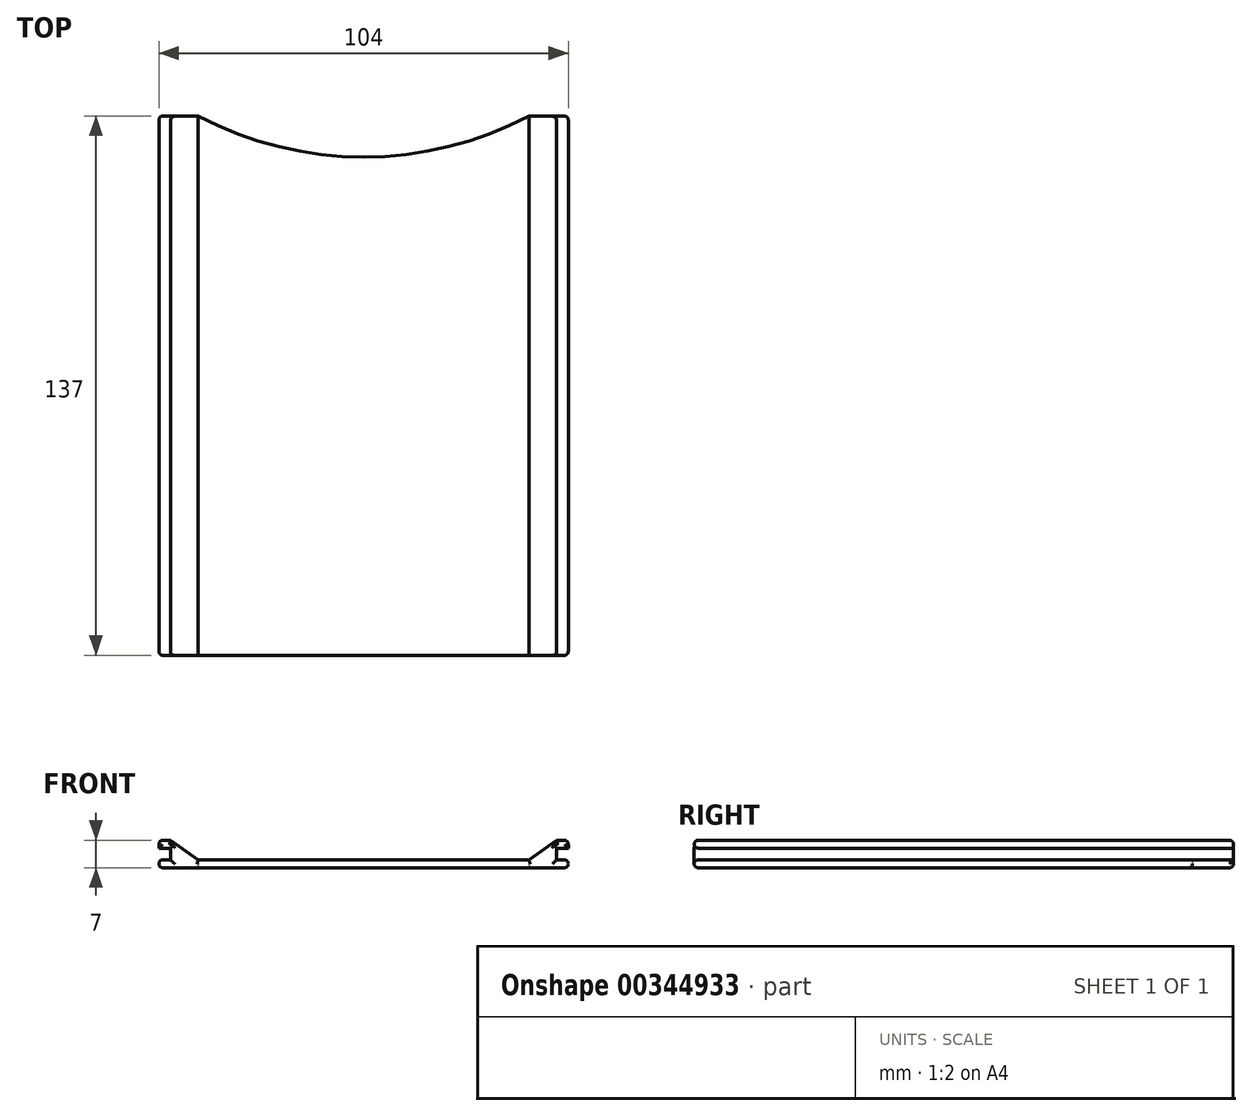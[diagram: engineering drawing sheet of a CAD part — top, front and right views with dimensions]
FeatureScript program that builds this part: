
annotation { "Feature Type Name" : "Feature", "Feature Type Description" : "" }
export const myFeature = defineFeature(function(context is Context, id is Id, definition is map)
    precondition{}
    {
        {
            var Q0;
            Q0=qCreatedBy(makeId("Top.planeOp"),FACE);
            var sketch = newSketch(context, id + "F0", { "sketchPlane" : qUnion([Q0])});
            skLineSegment(sketch, "E0", {"start": v(0, 0) * mm, "end": v(0, -68.5) * mm});
            skLineSegment(sketch, "E1", {"start": v(0, -68.5) * mm, "end": v(-52, -68.5) * mm});
            skLineSegment(sketch, "E2", {"start": v(-52, -68.5) * mm, "end": v(-52, 68.5) * mm});
            skLineSegment(sketch, "E3", {"start": v(-52, 68.5) * mm, "end": v(-42, 68.5) * mm});
            skLineSegment(sketch, "E4", {"start": v(0, -68.5) * mm, "end": v(52, -68.5) * mm});
            skLineSegment(sketch, "E5", {"start": v(52, -68.5) * mm, "end": v(52, 68.5) * mm});
            skLineSegment(sketch, "E6", {"start": v(52, 68.5) * mm, "end": v(42, 68.5) * mm});
            skArc(sketch, "E7", {"start": v(-42, 68.5) * mm, "mid": v(0, 58.1) * mm, "end": v(42, 68.5) * mm});
            skSolve(sketch);
        }
        {
            var Q0;
            Q0=makeQuery(id+"F0.imprint","IMPRINT",FACE,{"disambiguationData":[TD([[makeQuery(id+"F0.imprint","IMPRINT",EDGE,{"derivedFrom":sQuery(id+"F0.wireOp",EDGE,"E1")}),-1.0]])]});
            extrude(context, id + "F1", {"entities" : qUnion([Q0]), "depth" : 2 * mm});
        }
        {
            var Q0;
            Q0=makeQuery(id+"F1.opExtrude","CAP_FACE",FACE,{"disambiguationData":[OSD([sQuery(id+"F0.wireOp",EDGE,"E1"),sQuery(id+"F0.wireOp",EDGE,"E2"),sQuery(id+"F0.wireOp",EDGE,"E3"),sQuery(id+"F0.wireOp",EDGE,"E4"),sQuery(id+"F0.wireOp",EDGE,"E5"),sQuery(id+"F0.wireOp",EDGE,"E6"),sQuery(id+"F0.wireOp",EDGE,"E7")])],"isStart":false});
            var sketch = newSketch(context, id + "F2", { "sketchPlane" : qUnion([Q0])});
            skLineSegment(sketch, "E8.0", {"start": v(-42, -68.5) * mm, "end": v(-42, 68.5) * mm});
            skLineSegment(sketch, "E9.0", {"start": v(42, -68.5) * mm, "end": v(42, 68.5) * mm});
            skSolve(sketch);
        }
        {
            var Q0;
            {var subQ0=sQuery(id+"F2.wireOp",EDGE,"E8.0");Q0=makeQuery(id+"F2.imprint","IMPRINT",FACE,{"disambiguationData":[TD([[makeQuery(id+"F2.imprint","IMPRINT",EDGE,{"derivedFrom":subQ0}),1.0]])]});}
            var Q1;
            {var subQ0=sQuery(id+"F2.wireOp",EDGE,"E9.0");Q1=makeQuery(id+"F2.imprint","IMPRINT",FACE,{"disambiguationData":[TD([[makeQuery(id+"F2.imprint","IMPRINT",EDGE,{"derivedFrom":subQ0}),-1.0]])]});}
            extrude(context, id + "F3", {"entities" : qUnion([Q0, Q1]), "operationType" : NewBodyOperationType.ADD, "depth" : 5 * mm});
        }
        {
            var Q0;
            {var subQ0=sQuery(id+"F0.wireOp",EDGE,"E2");Q0=makeQuery(id+"F3.boolean.opBoolean","MERGE",FACE,{"derivedFrom":[makeQuery(id+"F1.opExtrude","SWEPT_FACE",FACE,{"disambiguationData":[OSD([subQ0])]}),makeQuery(id+"F3.opExtrude","SWEPT_FACE",FACE,{"disambiguationData":[OSD([subQ0])]})]});}
            var sketch = newSketch(context, id + "F4", { "sketchPlane" : qUnion([Q0])});
            skLineSegment(sketch, "E10.0", {"start": v(68.5, 5) * mm, "end": v(-68.5, 5) * mm});
            skLineSegment(sketch, "E11.0", {"start": v(68.5, 2) * mm, "end": v(-68.5, 2) * mm});
            skSolve(sketch);
        }
        {
            var Q0;
            {var subQ0=sQuery(id+"F4.wireOp",EDGE,"E10.0");Q0=makeQuery(id+"F4.imprint","IMPRINT",FACE,{"disambiguationData":[TD([[makeQuery(id+"F4.imprint","IMPRINT",EDGE,{"derivedFrom":subQ0}),1.0]])]});}
            extrude(context, id + "F5", {"entities" : qUnion([Q0]), "operationType" : NewBodyOperationType.REMOVE, "oppositeDirection" : true, "depth" : 3 * mm});
        }
        {
            var Q0;
            {var subQ0=sQuery(id+"F0.wireOp",EDGE,"E5");Q0=makeQuery(id+"F3.boolean.opBoolean","MERGE",FACE,{"derivedFrom":[makeQuery(id+"F1.opExtrude","SWEPT_FACE",FACE,{"disambiguationData":[OSD([subQ0])]}),makeQuery(id+"F3.opExtrude","SWEPT_FACE",FACE,{"disambiguationData":[OSD([subQ0])]})]});}
            var sketch = newSketch(context, id + "F6", { "sketchPlane" : qUnion([Q0])});
            skLineSegment(sketch, "E12.0", {"start": v(-68.5, 5) * mm, "end": v(68.5, 5) * mm});
            skLineSegment(sketch, "E13.0", {"start": v(-68.5, 2) * mm, "end": v(68.5, 2) * mm});
            skSolve(sketch);
        }
        {
            var Q0;
            {var subQ0=sQuery(id+"F6.wireOp",EDGE,"E12.0");Q0=makeQuery(id+"F6.imprint","IMPRINT",FACE,{"disambiguationData":[TD([[makeQuery(id+"F6.imprint","IMPRINT",EDGE,{"derivedFrom":subQ0}),-1.0]])]});}
            extrude(context, id + "F7", {"entities" : qUnion([Q0]), "operationType" : NewBodyOperationType.REMOVE, "oppositeDirection" : true, "depth" : 3 * mm});
        }
        {
            var Q0;
            Q0=makeQuery(id+"F3.opExtrude","CAP_EDGE",EDGE,{"disambiguationData":[OSD([sQuery(id+"F2.wireOp",EDGE,"E8.0")])],"isStart":false});
            chamfer(context, id + "F8", {"entities" : qUnion([Q0]), "chamferType" : ChamferType.TWO_OFFSETS, "width1" : 7 * mm, "oppositeDirection" : false, "width2" : 5 * mm, "tangentPropagation" : true});
        }
        {
            var Q0;
            Q0=makeQuery(id+"F3.opExtrude","CAP_EDGE",EDGE,{"disambiguationData":[OSD([sQuery(id+"F2.wireOp",EDGE,"E9.0")])],"isStart":false});
            chamfer(context, id + "F9", {"entities" : qUnion([Q0]), "chamferType" : ChamferType.TWO_OFFSETS, "width1" : 5 * mm, "oppositeDirection" : false, "width2" : 7 * mm, "tangentPropagation" : true});
        }
        {
            var Q0;
            Q0=makeQuery(id+"F7.boolean.opBoolean","COPY",EDGE,{"derivedFrom":makeQuery(id+"F7.opExtrude","CAP_EDGE",EDGE,{"disambiguationData":[OSD([sQuery(id+"F6.wireOp",EDGE,"E13.0")])],"isStart":true})});
            var Q1;
            Q1=makeQuery(id+"F1.opExtrude","CAP_EDGE",EDGE,{"disambiguationData":[OSD([sQuery(id+"F0.wireOp",EDGE,"E5")])],"isStart":true});
            var Q2;
            Q2=makeQuery(id+"F3.opExtrude","CAP_EDGE",EDGE,{"disambiguationData":[OSD([sQuery(id+"F0.wireOp",EDGE,"E5")])],"isStart":false});
            var Q3;
            Q3=makeQuery(id+"F7.boolean.opBoolean","COPY",EDGE,{"derivedFrom":makeQuery(id+"F7.opExtrude","CAP_EDGE",EDGE,{"disambiguationData":[OSD([sQuery(id+"F6.wireOp",EDGE,"E12.0")])],"isStart":true})});
            var Q4;
            Q4=makeQuery(id+"F3.opExtrude","CAP_EDGE",EDGE,{"disambiguationData":[OSD([sQuery(id+"F0.wireOp",EDGE,"E2")])],"isStart":false});
            var Q5;
            Q5=makeQuery(id+"F5.boolean.opBoolean","COPY",EDGE,{"derivedFrom":makeQuery(id+"F5.opExtrude","CAP_EDGE",EDGE,{"disambiguationData":[OSD([sQuery(id+"F4.wireOp",EDGE,"E10.0")])],"isStart":true})});
            var Q6;
            Q6=makeQuery(id+"F5.boolean.opBoolean","COPY",EDGE,{"derivedFrom":makeQuery(id+"F5.opExtrude","CAP_EDGE",EDGE,{"disambiguationData":[OSD([sQuery(id+"F4.wireOp",EDGE,"E11.0")])],"isStart":true})});
            var Q7;
            {var subQ0=sQuery(id+"F0.wireOp",EDGE,"E4");var subQ1=sQuery(id+"F0.wireOp",EDGE,"E1");var subQ2=makeQuery(id+"F1.opExtrude","CAP_EDGE",EDGE,{"disambiguationData":[OSD([subQ1,subQ0])],"isStart":false});Q7=makeQuery(id+"F3.boolean.opBoolean","MERGE",FACE,{"derivedFrom":[makeQuery(id+"F1.opExtrude","SWEPT_FACE",FACE,{"disambiguationData":[OSD([subQ1,subQ0])]}),makeQuery(id+"F3.opExtrude","SWEPT_FACE",FACE,{"disambiguationData":[OSD([subQ1,subQ0]),TDD([makeQuery(id+"F2.imprint","IMPRINT",EDGE,{"disambiguationData":[TD([[makeQuery(id+"F2.imprint","INTERSECT",VERTEX,{"derivedFrom":[subQ2,makeQuery(id+"F1.opExtrude","CAP_EDGE",EDGE,{"disambiguationData":[OSD([sQuery(id+"F0.wireOp",EDGE,"E2")])],"isStart":false})]}),1.0]])],"derivedFrom":subQ2})])]}),makeQuery(id+"F3.opExtrude","SWEPT_FACE",FACE,{"disambiguationData":[OSD([subQ1,subQ0]),TDD([makeQuery(id+"F2.imprint","IMPRINT",EDGE,{"disambiguationData":[TD([[makeQuery(id+"F2.imprint","INTERSECT",VERTEX,{"derivedFrom":[subQ2,makeQuery(id+"F1.opExtrude","CAP_EDGE",EDGE,{"disambiguationData":[OSD([sQuery(id+"F0.wireOp",EDGE,"E5")])],"isStart":false})]}),-1.0]])],"derivedFrom":subQ2})])]})]});}
            var Q8;
            Q8=makeQuery(id+"F3.opExtrude","CAP_EDGE",EDGE,{"disambiguationData":[OSD([sQuery(id+"F0.wireOp",EDGE,"E6")])],"isStart":false});
            var Q9;
            Q9=makeQuery(id+"F7.boolean.opBoolean","COPY",EDGE,{"derivedFrom":makeQuery(id+"F7.opExtrude","SWEPT_EDGE",EDGE,{"disambiguationData":[OSD([sQuery(id+"F0.wireOp",EDGE,"E5"),sQuery(id+"F0.wireOp",EDGE,"E6"),sQuery(id+"F6.wireOp",EDGE,"E12.0")])]})});
            var Q10;
            Q10=makeQuery(id+"F7.boolean.opBoolean","COPY",EDGE,{"derivedFrom":makeQuery(id+"F7.opExtrude","CAP_EDGE",EDGE,{"disambiguationData":[OSD([sQuery(id+"F0.wireOp",EDGE,"E5"),sQuery(id+"F0.wireOp",EDGE,"E6")])],"isStart":false})});
            var Q11;
            Q11=makeQuery(id+"F7.boolean.opBoolean","COPY",EDGE,{"derivedFrom":makeQuery(id+"F7.opExtrude","SWEPT_EDGE",EDGE,{"disambiguationData":[OSD([sQuery(id+"F0.wireOp",EDGE,"E5"),sQuery(id+"F0.wireOp",EDGE,"E6"),sQuery(id+"F6.wireOp",EDGE,"E13.0")])]})});
            var Q12;
            Q12=makeQuery(id+"F1.opExtrude","CAP_EDGE",EDGE,{"disambiguationData":[OSD([sQuery(id+"F0.wireOp",EDGE,"E6")])],"isStart":true});
            var Q13;
            {var subQ0=sQuery(id+"F0.wireOp",EDGE,"E5");var subQ1=sQuery(id+"F0.wireOp",EDGE,"E6");Q13=makeQuery(id+"F7.boolean.opBoolean","SPLIT",EDGE,{"disambiguationData":[TD([makeQuery(id+"F7.opExtrude","SWEPT_FACE",FACE,{"disambiguationData":[OSD([sQuery(id+"F6.wireOp",EDGE,"E13.0")])]})])],"derivedFrom":makeQuery(id+"F3.boolean.opBoolean","MERGE",EDGE,{"derivedFrom":[makeQuery(id+"F1.opExtrude","SWEPT_EDGE",EDGE,{"disambiguationData":[OSD([subQ0,subQ1])]}),makeQuery(id+"F3.opExtrude","SWEPT_EDGE",EDGE,{"disambiguationData":[OSD([subQ0,subQ1])]})]})});}
            var Q14;
            {var subQ0=sQuery(id+"F0.wireOp",EDGE,"E6");var subQ1=sQuery(id+"F0.wireOp",EDGE,"E5");Q14=makeQuery(id+"F7.boolean.opBoolean","SPLIT",EDGE,{"disambiguationData":[TD([makeQuery(id+"F7.opExtrude","SWEPT_FACE",FACE,{"disambiguationData":[OSD([sQuery(id+"F6.wireOp",EDGE,"E12.0")])]})])],"derivedFrom":makeQuery(id+"F3.boolean.opBoolean","MERGE",EDGE,{"derivedFrom":[makeQuery(id+"F1.opExtrude","SWEPT_EDGE",EDGE,{"disambiguationData":[OSD([subQ1,subQ0])]}),makeQuery(id+"F3.opExtrude","SWEPT_EDGE",EDGE,{"disambiguationData":[OSD([subQ1,subQ0])]})]})});}
            var Q15;
            Q15=makeQuery(id+"F1.opExtrude","CAP_EDGE",EDGE,{"disambiguationData":[OSD([sQuery(id+"F0.wireOp",EDGE,"E7")])],"isStart":true});
            var Q16;
            Q16=makeQuery(id+"F1.opExtrude","CAP_EDGE",EDGE,{"disambiguationData":[OSD([sQuery(id+"F0.wireOp",EDGE,"E3")])],"isStart":true});
            var Q17;
            Q17=makeQuery(id+"F1.opExtrude","CAP_EDGE",EDGE,{"disambiguationData":[OSD([sQuery(id+"F0.wireOp",EDGE,"E2")])],"isStart":true});
            var Q18;
            Q18=makeQuery(id+"F5.boolean.opBoolean","COPY",EDGE,{"derivedFrom":makeQuery(id+"F5.opExtrude","SWEPT_EDGE",EDGE,{"disambiguationData":[OSD([sQuery(id+"F0.wireOp",EDGE,"E2"),sQuery(id+"F0.wireOp",EDGE,"E3"),sQuery(id+"F4.wireOp",EDGE,"E11.0")])]})});
            var Q19;
            Q19=makeQuery(id+"F5.boolean.opBoolean","COPY",EDGE,{"derivedFrom":makeQuery(id+"F5.opExtrude","CAP_EDGE",EDGE,{"disambiguationData":[OSD([sQuery(id+"F0.wireOp",EDGE,"E2"),sQuery(id+"F0.wireOp",EDGE,"E3")])],"isStart":false})});
            var Q20;
            Q20=makeQuery(id+"F5.boolean.opBoolean","COPY",EDGE,{"derivedFrom":makeQuery(id+"F5.opExtrude","SWEPT_EDGE",EDGE,{"disambiguationData":[OSD([sQuery(id+"F0.wireOp",EDGE,"E2"),sQuery(id+"F0.wireOp",EDGE,"E3"),sQuery(id+"F4.wireOp",EDGE,"E10.0")])]})});
            var Q21;
            {var subQ0=sQuery(id+"F0.wireOp",EDGE,"E3");var subQ1=sQuery(id+"F0.wireOp",EDGE,"E2");Q21=makeQuery(id+"F5.boolean.opBoolean","SPLIT",EDGE,{"disambiguationData":[TD([makeQuery(id+"F5.opExtrude","SWEPT_FACE",FACE,{"disambiguationData":[OSD([sQuery(id+"F4.wireOp",EDGE,"E10.0")])]})])],"derivedFrom":makeQuery(id+"F3.boolean.opBoolean","MERGE",EDGE,{"derivedFrom":[makeQuery(id+"F1.opExtrude","SWEPT_EDGE",EDGE,{"disambiguationData":[OSD([subQ1,subQ0])]}),makeQuery(id+"F3.opExtrude","SWEPT_EDGE",EDGE,{"disambiguationData":[OSD([subQ1,subQ0])]})]})});}
            var Q22;
            Q22=makeQuery(id+"F3.opExtrude","CAP_EDGE",EDGE,{"disambiguationData":[OSD([sQuery(id+"F0.wireOp",EDGE,"E3")])],"isStart":false});
            var Q23;
            {var subQ0=sQuery(id+"F0.wireOp",EDGE,"E2");var subQ1=sQuery(id+"F0.wireOp",EDGE,"E3");Q23=makeQuery(id+"F5.boolean.opBoolean","SPLIT",EDGE,{"disambiguationData":[TD([makeQuery(id+"F5.opExtrude","SWEPT_FACE",FACE,{"disambiguationData":[OSD([sQuery(id+"F4.wireOp",EDGE,"E11.0")])]})])],"derivedFrom":makeQuery(id+"F3.boolean.opBoolean","MERGE",EDGE,{"derivedFrom":[makeQuery(id+"F1.opExtrude","SWEPT_EDGE",EDGE,{"disambiguationData":[OSD([subQ0,subQ1])]}),makeQuery(id+"F3.opExtrude","SWEPT_EDGE",EDGE,{"disambiguationData":[OSD([subQ0,subQ1])]})]})});}
            fillet(context, id + "F10", {"entities" : qUnion([Q0, Q1, Q2, Q3, Q4, Q5, Q6, Q7, Q8, Q9, Q10, Q11, Q12, Q13, Q14, Q15, Q16, Q17, Q18, Q19, Q20, Q21, Q22, Q23]), "radius" : 1 * mm, "tangentPropagation" : true, "allowEdgeOverflow" : false});
        }
    });
